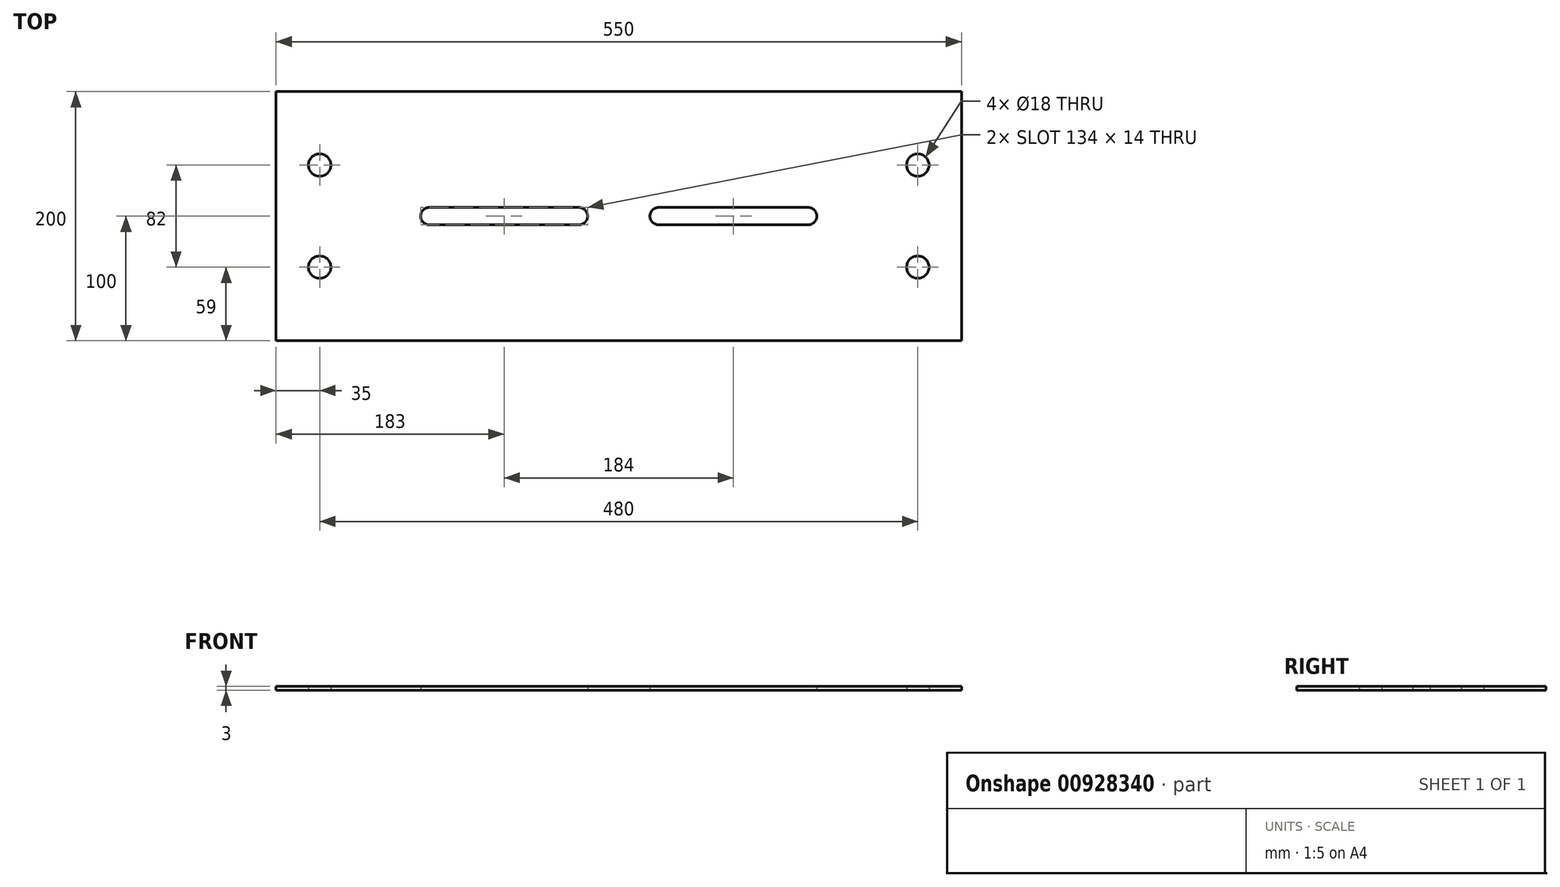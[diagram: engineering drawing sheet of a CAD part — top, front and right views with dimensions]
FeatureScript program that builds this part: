
annotation { "Feature Type Name" : "Feature", "Feature Type Description" : "" }
export const myFeature = defineFeature(function(context is Context, id is Id, definition is map)
    precondition{}
    {
        {
            var Q0;
            Q0=qCreatedBy(makeId("Top.planeOp"),FACE);
            var sketch = newSketch(context, id + "F0", { "sketchPlane" : qUnion([Q0])});
            skLineSegment(sketch, "E0.bottom", {"start": v(280.8, 102.3) * mm, "end": v(-269.2, 102.3) * mm});
            skLineSegment(sketch, "E0.top", {"start": v(280.8, -97.7) * mm, "end": v(-269.2, -97.7) * mm});
            skLineSegment(sketch, "E0.left", {"start": v(280.8, 102.3) * mm, "end": v(280.8, -97.7) * mm});
            skLineSegment(sketch, "E0.right", {"start": v(-269.2, 102.3) * mm, "end": v(-269.2, -97.7) * mm});
            skPoint(sketch, "E0.middle", {"position": v(5.8, 2.3) * mm});
            skCircle(sketch, "E1", {"center": v(-234.2, 43.3) * mm, "radius": 9 * mm});
            skLineSegment(sketch, "E2", {"start": v(97.8, -64.68) * mm, "end": v(97.8, 59.65) * mm, "construction": true});
            skLineSegment(sketch, "E3", {"start": v(37.8, 9.3) * mm, "end": v(157.8, 9.3) * mm});
            skCircle(sketch, "E4.MirrorC", {"center": v(-234.2, -38.7) * mm, "radius": 9 * mm});
            skCircle(sketch, "E5.MirrorC", {"center": v(245.8, -38.7) * mm, "radius": 9 * mm});
            skCircle(sketch, "E6.MirrorC", {"center": v(245.8, 43.3) * mm, "radius": 9 * mm});
            skLineSegment(sketch, "E7.MirrorCS", {"start": v(37.8, -4.7) * mm, "end": v(157.8, -4.7) * mm});
            skLineSegment(sketch, "E8", {"start": v(37.8, 9.3) * mm, "end": v(37.8, -4.7) * mm, "construction": true});
            skArc(sketch, "E9", {"start": v(37.8, 9.3) * mm, "mid": v(30.8, 2.3) * mm, "end": v(37.8, -4.7) * mm});
            skArc(sketch, "E10.MirrorCS", {"start": v(157.8, 9.3) * mm, "mid": v(164.8, 2.3) * mm, "end": v(157.8, -4.7) * mm});
            skArc(sketch, "E11.MirrorCS", {"start": v(-26.2, 9.3) * mm, "mid": v(-19.2, 2.3) * mm, "end": v(-26.2, -4.7) * mm});
            skLineSegment(sketch, "E12.MirrorCS", {"start": v(-26.2, -4.7) * mm, "end": v(-146.2, -4.7) * mm});
            skLineSegment(sketch, "E13.MirrorCS", {"start": v(-26.2, 9.3) * mm, "end": v(-146.2, 9.3) * mm});
            skArc(sketch, "E14.MirrorCS", {"start": v(-146.2, 9.3) * mm, "mid": v(-153.2, 2.3) * mm, "end": v(-146.2, -4.7) * mm});
            skSolve(sketch);
        }
        {
            var Q0;
            Q0=makeQuery(id+"F0.imprint","IMPRINT",FACE,{"disambiguationData":[TD([[makeQuery(id+"F0.imprint","IMPRINT",EDGE,{"derivedFrom":sQuery(id+"F0.wireOp",EDGE,"E0.bottom")}),1.0]])]});
            extrude(context, id + "F1", {"entities" : qUnion([Q0]), "depth" : 3 * mm, "offsetDistance" : 25 * mm});
        }
    });
